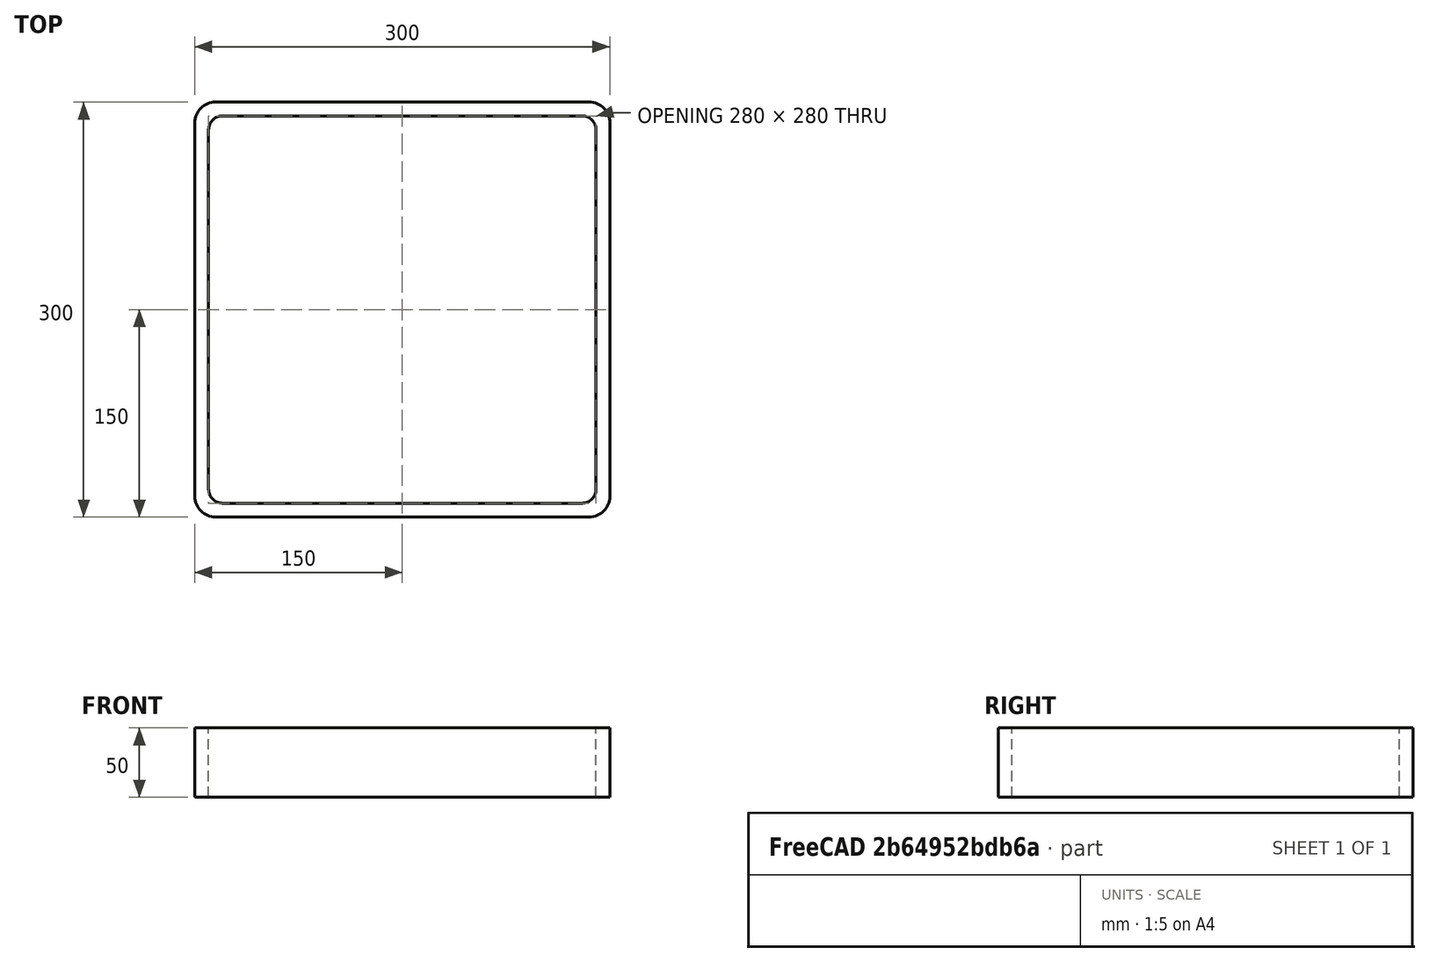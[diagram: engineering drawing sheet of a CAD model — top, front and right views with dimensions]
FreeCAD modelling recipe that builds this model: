
FCSTD DOCUMENT  (FreeCAD 0.15R4671 (Git))
Label: Square hollow section 300x300x10 EN10219 S235JRH
License: All rights reserved
LicenseURL: http://en.wikipedia.org/wiki/All_rights_reserved
objects: Sketcher::SketchObject×1, Part::Extrusion×1
note: 2 computed .brp shape members not serialized (recipe doc carries the construction recipe); baked Part::Feature solids carry a one-line shape summary decoded from their .brp

FEATURE [Sketcher::SketchObject] Sketch
  sketch-geometry (16):
    g0: LineSegment StartX=-130 StartY=140 StartZ=0 EndX=130 EndY=140 EndZ=0
    g1: LineSegment StartX=140 StartY=130 StartZ=0 EndX=140 EndY=-130 EndZ=0
    g2: LineSegment StartX=130 StartY=-140 StartZ=0 EndX=-130 EndY=-140 EndZ=0
    g3: LineSegment StartX=-140 StartY=-130 StartZ=0 EndX=-140 EndY=130 EndZ=0
    g4: LineSegment StartX=-135 StartY=150 StartZ=0 EndX=135 EndY=150 EndZ=0
    g5: LineSegment StartX=150 StartY=135 StartZ=0 EndX=150 EndY=-135 EndZ=0
    g6: LineSegment StartX=135 StartY=-150 StartZ=0 EndX=-135 EndY=-150 EndZ=0
    g7: LineSegment StartX=-150 StartY=-135 StartZ=0 EndX=-150 EndY=135 EndZ=0
    g8: ArcOfCircle CenterX=-130 CenterY=130 CenterZ=0 NormalX=0 NormalY=0 NormalZ=1 Radius=10 StartAngle=1.5708 EndAngle=3.14159
    g9: ArcOfCircle CenterX=130 CenterY=130 CenterZ=0 NormalX=0 NormalY=0 NormalZ=1 Radius=10 StartAngle=0 EndAngle=1.5708
    g10: ArcOfCircle CenterX=130 CenterY=-130 CenterZ=0 NormalX=0 NormalY=0 NormalZ=1 Radius=10 StartAngle=4.71239 EndAngle=6.28319
    g11: ArcOfCircle CenterX=-130 CenterY=-130 CenterZ=0 NormalX=0 NormalY=0 NormalZ=1 Radius=10 StartAngle=3.14159 EndAngle=4.71239
    g12: ArcOfCircle CenterX=135 CenterY=135 CenterZ=0 NormalX=0 NormalY=0 NormalZ=1 Radius=15 StartAngle=0 EndAngle=1.5708
    g13: ArcOfCircle CenterX=135 CenterY=-135 CenterZ=0 NormalX=0 NormalY=0 NormalZ=1 Radius=15 StartAngle=4.71239 EndAngle=6.28319
    g14: ArcOfCircle CenterX=-135 CenterY=-135 CenterZ=0 NormalX=0 NormalY=0 NormalZ=1 Radius=15 StartAngle=3.14159 EndAngle=4.71239
    g15: ArcOfCircle CenterX=-135 CenterY=135 CenterZ=0 NormalX=0 NormalY=0 NormalZ=1 Radius=15 StartAngle=1.5708 EndAngle=3.14159
  constraints (36):
    c: Horizontal(g2)
    c: Vertical(g3)
    c: Horizontal(g6)
    c: Vertical(g7)
    c: Tangent(g3,g8) = 1.5708
    c: Tangent(g0,g8) = 1.5708
    c: Tangent(g0,g9) = 1.5708
    c: Tangent(g1,g9) = 1.5708
    c: Tangent(g1,g10) = 1.5708
    c: Tangent(g2,g10) = 1.5708
    c: Tangent(g2,g11) = 1.5708
    c: Tangent(g3,g11) = 1.5708
    c: Tangent(g4,g12) = 1.5708
    c: Tangent(g5,g12) = 1.5708
    c: Tangent(g5,g13) = 1.5708
    c: Tangent(g6,g13) = 1.5708
    c: Tangent(g6,g14) = 1.5708
    c: Tangent(g7,g14) = 1.5708
    c: Tangent(g7,g15) = 1.5708
    c: Tangent(g4,g15) = 1.5708
    c: Equal(g9,g8)
    c: Equal(g9,g11)
    c: Equal(g9,g10)
    c: Equal(g12,g15)
    c: Equal(g12,g14)
    c: Equal(g12,g13)
    c: Symmetric(g4,g6,g-1)
    c: Symmetric(g7,g5,g-2)
    c: DistanceY(g4,g6) = -300
    c: DistanceX(g7,g5) = 300
    c: Symmetric(g3,g1,g-2)
    c: Symmetric(g0,g2,g-1)
    c: DistanceY(g0,g4) = 10
    c: DistanceX(g5,g1) = -10
    c: Radius(g9) = 10
    c: Radius(g12) = 15
FEATURE [Part::Extrusion] Extrude  label="Square hollow section 300x300x10 EN10219 S235JRH"
  Base = -> Sketch
  Dir = (0,0,50)
  Solid = true
